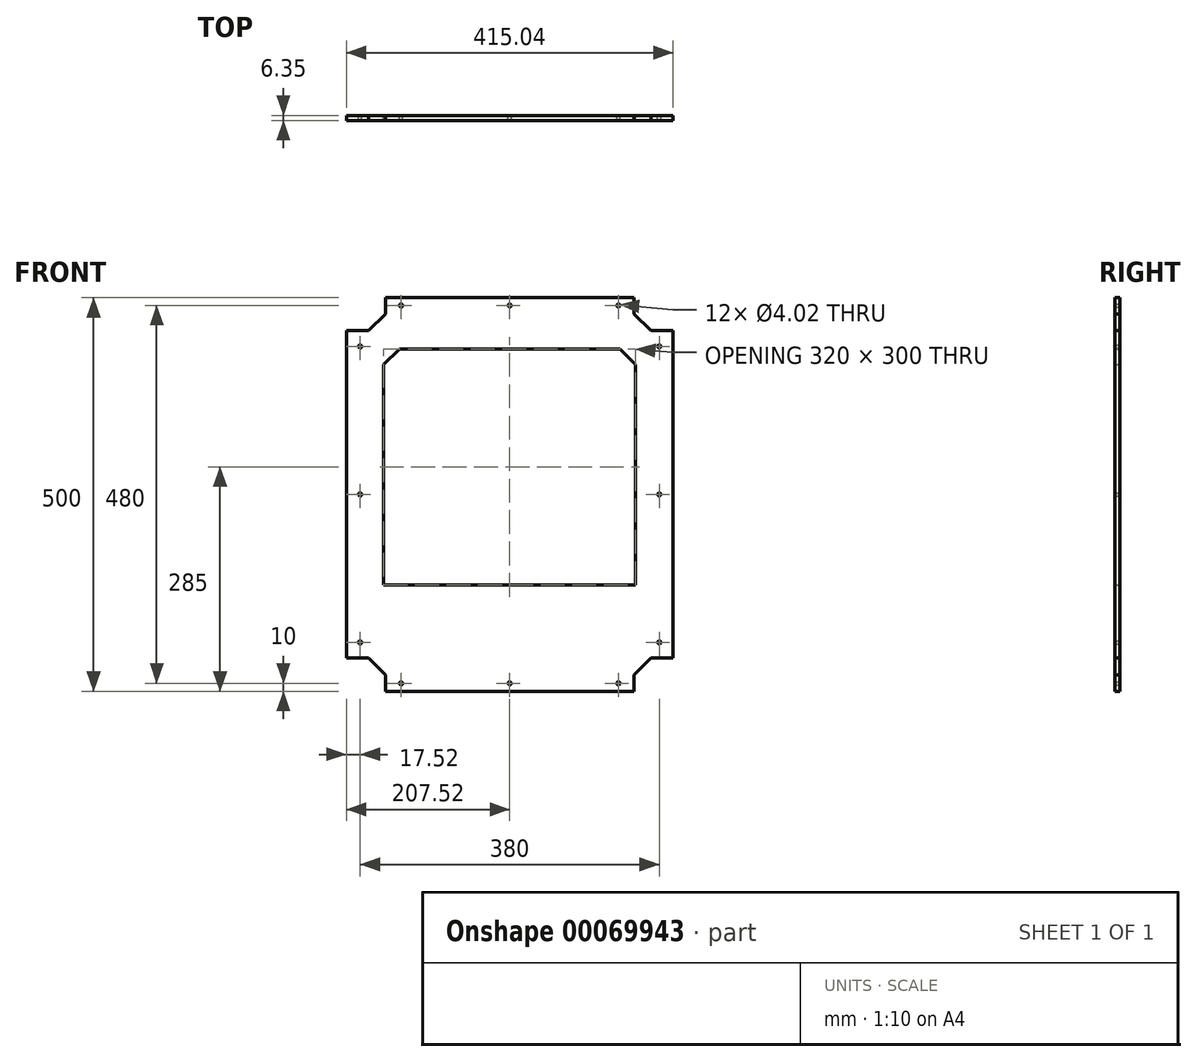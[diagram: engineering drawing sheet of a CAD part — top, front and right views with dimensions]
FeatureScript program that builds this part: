
annotation { "Feature Type Name" : "Feature", "Feature Type Description" : "" }
export const myFeature = defineFeature(function(context is Context, id is Id, definition is map)
    precondition{}
    {
        {
            var Q0;
            Q0=qCreatedBy(makeId("Front.planeOp"),FACE);
            var sketch = newSketch(context, id + "F0", { "sketchPlane" : qUnion([Q0])});
            skLineSegment(sketch, "E0", {"start": v(0, 0) * mm, "end": v(180, 0) * mm, "construction": true});
            skLineSegment(sketch, "E1", {"start": v(0, 0) * mm, "end": v(0, -230) * mm, "construction": true});
            skLineSegment(sketch, "E2", {"start": v(0, 0) * mm, "end": v(-180, 0) * mm, "construction": true});
            skLineSegment(sketch, "E3", {"start": v(0, 0) * mm, "end": v(0, 230) * mm, "construction": true});
            skLineSegment(sketch, "E4", {"start": v(0, 230) * mm, "end": v(160, 230) * mm, "construction": true});
            skLineSegment(sketch, "E5", {"start": v(0, 230) * mm, "end": v(-160, 230) * mm, "construction": true});
            skLineSegment(sketch, "E6", {"start": v(0, -230) * mm, "end": v(160, -230) * mm, "construction": true});
            skLineSegment(sketch, "E7", {"start": v(0, -230) * mm, "end": v(-160, -230) * mm, "construction": true});
            skLineSegment(sketch, "E8", {"start": v(-180, 0) * mm, "end": v(-180, -210) * mm, "construction": true});
            skLineSegment(sketch, "E9", {"start": v(-180, 0) * mm, "end": v(-180, 210) * mm, "construction": true});
            skLineSegment(sketch, "E10", {"start": v(180, 0) * mm, "end": v(180, 210) * mm, "construction": true});
            skLineSegment(sketch, "E11", {"start": v(180, 0) * mm, "end": v(180, -210) * mm, "construction": true});
            skLineSegment(sketch, "E12", {"start": v(-180, 210) * mm, "end": v(-160, 230) * mm, "construction": true});
            skLineSegment(sketch, "E13", {"start": v(160, 230) * mm, "end": v(180, 210) * mm, "construction": true});
            skLineSegment(sketch, "E14", {"start": v(-180, -210) * mm, "end": v(-160, -230) * mm, "construction": true});
            skLineSegment(sketch, "E15", {"start": v(160, -230) * mm, "end": v(180, -210) * mm, "construction": true});
            skLineSegment(sketch, "E16", {"start": v(140, 230) * mm, "end": v(140, 185) * mm, "construction": true});
            skLineSegment(sketch, "E17", {"start": v(140, 185) * mm, "end": v(180, 185) * mm, "construction": true});
            skLineSegment(sketch, "E18", {"start": v(-140, 230) * mm, "end": v(-140, 185) * mm, "construction": true});
            skLineSegment(sketch, "E19", {"start": v(-140, 185) * mm, "end": v(-180, 185) * mm, "construction": true});
            skLineSegment(sketch, "E20", {"start": v(170, 220) * mm, "end": v(168.59, 218.59) * mm, "construction": true});
            skLineSegment(sketch, "E21", {"start": v(180, 210) * mm, "end": v(200, 210) * mm, "construction": true});
            skLineSegment(sketch, "E22", {"start": v(190, 210) * mm, "end": v(190, 208) * mm, "construction": true});
            skLineSegment(sketch, "E23", {"start": v(160, 230) * mm, "end": v(160, 250) * mm, "construction": true});
            skLineSegment(sketch, "E24", {"start": v(180, -210) * mm, "end": v(200, -210) * mm, "construction": true});
            skLineSegment(sketch, "E25", {"start": v(160, -230) * mm, "end": v(160, -250) * mm, "construction": true});
            skLineSegment(sketch, "E26", {"start": v(-180, -210) * mm, "end": v(-200, -210) * mm, "construction": true});
            skLineSegment(sketch, "E27", {"start": v(-160, -230) * mm, "end": v(-160, -250) * mm, "construction": true});
            skLineSegment(sketch, "E28", {"start": v(190, -210) * mm, "end": v(190, -208) * mm, "construction": true});
            skLineSegment(sketch, "E29", {"start": v(160, -240) * mm, "end": v(158, -240) * mm, "construction": true});
            skLineSegment(sketch, "E30", {"start": v(170, -220) * mm, "end": v(168.59, -218.59) * mm, "construction": true});
            skLineSegment(sketch, "E31", {"start": v(168.59, -218.59) * mm, "end": v(179.17, -208) * mm});
            skLineSegment(sketch, "E32", {"start": v(168.59, -218.59) * mm, "end": v(158, -229.17) * mm});
            skLineSegment(sketch, "E33", {"start": v(158, -240) * mm, "end": v(158, -229.17) * mm});
            skLineSegment(sketch, "E34", {"start": v(158, -240) * mm, "end": v(158, -250) * mm});
            skLineSegment(sketch, "E35", {"start": v(168.59, 218.59) * mm, "end": v(179.17, 208) * mm});
            skLineSegment(sketch, "E36", {"start": v(168.59, 218.59) * mm, "end": v(158, 229.17) * mm});
            skLineSegment(sketch, "E37", {"start": v(160, 240) * mm, "end": v(158, 240) * mm, "construction": true});
            skPoint(sketch, "E37.endSnap0", {"position": v(160, 240) * mm});
            skLineSegment(sketch, "E38", {"start": v(158, 240) * mm, "end": v(158, 229.17) * mm});
            skLineSegment(sketch, "E39", {"start": v(-160, -240) * mm, "end": v(-158, -240) * mm, "construction": true});
            skLineSegment(sketch, "E40", {"start": v(-170, -220) * mm, "end": v(-168.59, -218.59) * mm, "construction": true});
            skLineSegment(sketch, "E41", {"start": v(-190, -210) * mm, "end": v(-190, -208) * mm, "construction": true});
            skPoint(sketch, "E41.endSnap0", {"position": v(-190, -210) * mm});
            skLineSegment(sketch, "E42", {"start": v(-168.59, -218.59) * mm, "end": v(-157.17, -230) * mm});
            skLineSegment(sketch, "E43", {"start": v(-158, -240) * mm, "end": v(-158, -229.17) * mm});
            skLineSegment(sketch, "E44", {"start": v(-168.59, -218.59) * mm, "end": v(-179.17, -208) * mm});
            skLineSegment(sketch, "E45", {"start": v(-158, -240) * mm, "end": v(-158, -250) * mm});
            skLineSegment(sketch, "E46", {"start": v(-158, -250) * mm, "end": v(158, -250) * mm});
            skLineSegment(sketch, "E47", {"start": v(-160, 230) * mm, "end": v(-160, 250) * mm, "construction": true});
            skLineSegment(sketch, "E48", {"start": v(-180, 210) * mm, "end": v(-200, 210) * mm, "construction": true});
            skLineSegment(sketch, "E49", {"start": v(-160, 240) * mm, "end": v(-158, 240) * mm, "construction": true});
            skLineSegment(sketch, "E50", {"start": v(-170, 220) * mm, "end": v(-168.59, 218.59) * mm, "construction": true});
            skLineSegment(sketch, "E51", {"start": v(-190, 210) * mm, "end": v(-190, 208) * mm, "construction": true});
            skLineSegment(sketch, "E52", {"start": v(-168.59, 218.59) * mm, "end": v(-179.17, 208) * mm});
            skLineSegment(sketch, "E53", {"start": v(-168.59, 218.59) * mm, "end": v(-158, 229.17) * mm});
            skLineSegment(sketch, "E54", {"start": v(-158, 240) * mm, "end": v(-158, 229.17) * mm});
            skLineSegment(sketch, "E55", {"start": v(-158, 240) * mm, "end": v(-158, 250) * mm});
            skLineSegment(sketch, "E56", {"start": v(-158, 250) * mm, "end": v(158, 250) * mm});
            skLineSegment(sketch, "E57", {"start": v(158, 250) * mm, "end": v(158, 240) * mm});
            skLineSegment(sketch, "E58", {"start": v(158, 240) * mm, "end": v(-158, 240) * mm, "construction": true});
            skLineSegment(sketch, "E59", {"start": v(-190, 208) * mm, "end": v(-190, -208) * mm, "construction": true});
            skLineSegment(sketch, "E60", {"start": v(-158, -240) * mm, "end": v(158, -240) * mm, "construction": true});
            skLineSegment(sketch, "E61", {"start": v(190, -208) * mm, "end": v(190, 208) * mm, "construction": true});
            skLineSegment(sketch, "E62", {"start": v(-168.59, 218.59) * mm, "end": v(-129.7, 179.7) * mm, "construction": true});
            skLineSegment(sketch, "E63", {"start": v(168.59, 218.59) * mm, "end": v(129.7, 179.7) * mm, "construction": true});
            skLineSegment(sketch, "E64", {"start": v(140, 185) * mm, "end": v(160, 165) * mm});
            skLineSegment(sketch, "E65", {"start": v(160, 165) * mm, "end": v(180, 165) * mm, "construction": true});
            skLineSegment(sketch, "E66", {"start": v(140, 185) * mm, "end": v(-140, 185) * mm});
            skLineSegment(sketch, "E67", {"start": v(-140, 185) * mm, "end": v(-160, 165) * mm});
            skLineSegment(sketch, "E68", {"start": v(-160, 165) * mm, "end": v(-180, 165) * mm, "construction": true});
            skLineSegment(sketch, "E69", {"start": v(-160, 165) * mm, "end": v(-160, -115) * mm});
            skLineSegment(sketch, "E70", {"start": v(0, -115) * mm, "end": v(-160, -115) * mm});
            skLineSegment(sketch, "E71", {"start": v(0, -115) * mm, "end": v(160, -115) * mm});
            skLineSegment(sketch, "E72", {"start": v(160, -115) * mm, "end": v(160, 165) * mm});
            skCircle(sketch, "E73", {"center": v(0, -240) * mm, "radius": 2 * mm});
            skCircle(sketch, "E74", {"center": v(138, -240) * mm, "radius": 2 * mm});
            skCircle(sketch, "E75", {"center": v(-138, -240) * mm, "radius": 2 * mm});
            skCircle(sketch, "E76", {"center": v(190, -188) * mm, "radius": 2 * mm});
            skCircle(sketch, "E77", {"center": v(190, 0) * mm, "radius": 2 * mm});
            skCircle(sketch, "E78", {"center": v(190, 188) * mm, "radius": 2 * mm});
            skCircle(sketch, "E79", {"center": v(0, 240) * mm, "radius": 2 * mm});
            skCircle(sketch, "E80", {"center": v(138, 240) * mm, "radius": 2 * mm});
            skCircle(sketch, "E81", {"center": v(-138, 240) * mm, "radius": 2 * mm});
            skCircle(sketch, "E82", {"center": v(-190, 188) * mm, "radius": 2 * mm});
            skCircle(sketch, "E83", {"center": v(-190, 0) * mm, "radius": 2 * mm});
            skCircle(sketch, "E84", {"center": v(-190, -188) * mm, "radius": 2 * mm});
            skLineSegment(sketch, "E85", {"start": v(-179.17, 208) * mm, "end": v(-207.52, 208) * mm});
            skLineSegment(sketch, "E86", {"start": v(-207.52, 208) * mm, "end": v(-207.52, -208) * mm});
            skLineSegment(sketch, "E87", {"start": v(-207.52, -208) * mm, "end": v(-179.17, -208) * mm});
            skLineSegment(sketch, "E88", {"start": v(179.17, -208) * mm, "end": v(207.52, -208) * mm});
            skLineSegment(sketch, "E89", {"start": v(207.52, -208) * mm, "end": v(207.52, 208) * mm});
            skLineSegment(sketch, "E90", {"start": v(207.52, 208) * mm, "end": v(179.17, 208) * mm});
            skSolve(sketch);
        }
        {
            var Q0;
            Q0=makeQuery(id+"F0.imprint","IMPRINT",FACE,{"disambiguationData":[TD([[makeQuery(id+"F0.imprint","IMPRINT",EDGE,{"derivedFrom":sQuery(id+"F0.wireOp",EDGE,"C4Y7uumh-JBdU-wd9B-4kXg-IEDmNJMjGin5")}),1.0]])]});
            var Q1;
            Q1=qSketchRegion(id+"F0",true);
            extrude(context, id + "F1", {"entities" : qUnion([Q0, Q1]), "depth" : 6.35 * mm});
        }
    });
